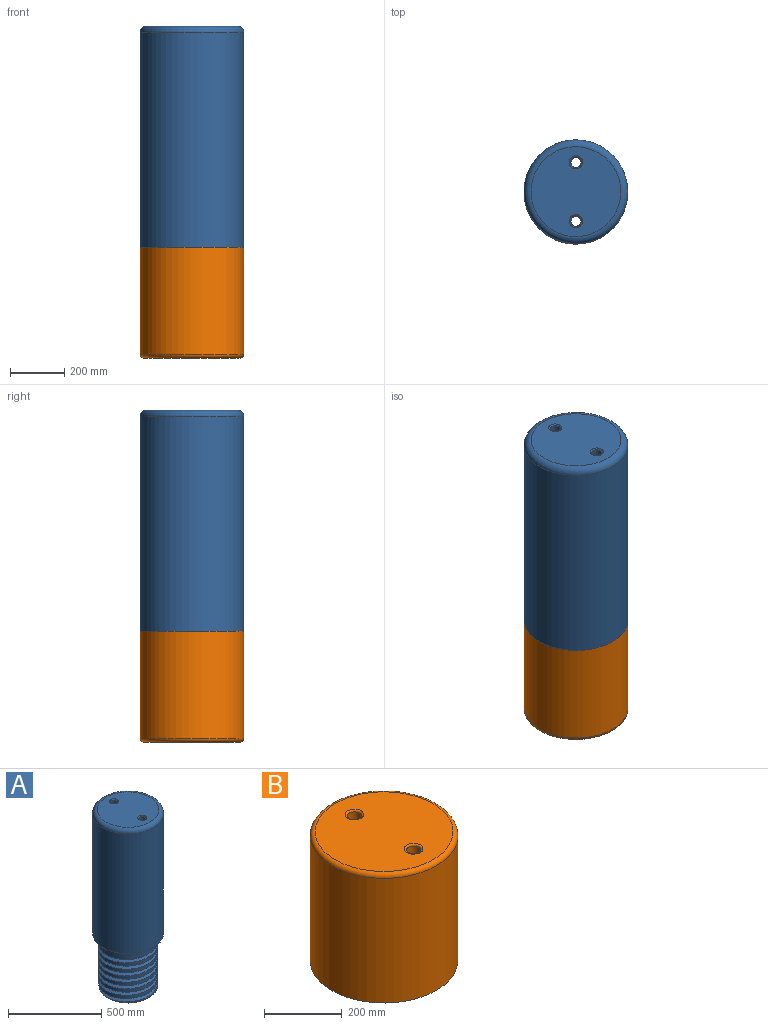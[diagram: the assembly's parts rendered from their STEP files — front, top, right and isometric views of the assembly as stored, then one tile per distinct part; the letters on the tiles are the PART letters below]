
ASSEMBLY  parts=2 mates=1
PART A: 25 faces, bbox 413.1x413.1x1182.3 mm
  f0: cylinder r=158.75mm len=317.5mm, axis (0,0,1), area 66109.5mm2, adj f1,f10,f15,f16
  f1: cylinder r=158.75mm len=317.5mm, axis (0,0,1), area 22484.7mm2, adj f0,f2,f16,f17
  f2: cylinder r=158.75mm len=317.5mm, axis (0,0,1), area 22483.1mm2, adj f1,f3,f16,f17
  f3: cylinder r=158.75mm len=317.5mm, axis (0,0,1), area 22485.4mm2, adj f2,f4,f16,f17
  f4: cylinder r=158.75mm len=317.5mm, axis (0,0,1), area 22483.2mm2, adj f3,f5,f16,f17
  f5: cylinder r=158.75mm len=317.5mm, axis (0,0,1), area 22482.8mm2, adj f4,f6,f16,f17
  f6: cylinder r=158.75mm len=317.5mm, axis (0,0,1), area 22438.2mm2, adj f5,f7,f14,f16,f17
  f7: cylinder r=158.75mm len=316.18mm, axis (0,0,1), area 4915.2mm2, adj f6,f14,f17
  f8: cylinder r=190.5mm len=787.4mm, axis (0,0,-1), area 942475.9mm2, adj f10,f18
  f9: plane 330.2x330.2mm, normal (0,0,1), area 81975.1mm2, adj f18,f23,f24
  f10: plane 381x381mm, normal (0,0,-1), area 34836.1mm2, adj f0,f8
  f11: plane 292.85x289.41mm, normal (0,0,-1), area 10854.2mm2, adj f13,f14,f16,f17
  f12: plane 266.7x266.7mm, normal (0,0,-1), area 52206.1mm2, adj f13,f21,f22
  f13: cylinder r=133.35mm len=1117.6mm, axis (0,0,1), area 936395.4mm2, adj f11,f12
  f14: cone r=146.05mm half-angle=45deg, axis (0,0,1), area 11945.9mm2, adj f6,f7,f11,f16,f17
  f15: plane 20.32x17.6mm, normal (0,-1,0), area 178.8mm2, adj f0,f16,f17
  f16: bspline ~317.5x317.5mm, area 134574.2mm2, adj f0,f1,f2,f3,f4,f5,f6,f11
  f17: bspline ~317.5x317.5mm, area 130072.8mm2, adj f1,f2,f3,f4,f5,f6,f7,f11
  f18: torus R=165.1mm, axis (0,0,1), area 45442.2mm2, adj f8,f9
  f19: cylinder r=19.05mm len=40.64mm, axis (0,0,1), area 4864.4mm2, adj f22,f23
  f20: cylinder r=19.05mm len=40.64mm, axis (0,0,1), area 4864.4mm2, adj f21,f24
  f21: torus R=24.13mm, axis (0,0,1), area 1047.7mm2, adj f12,f20
  f22: torus R=24.13mm, axis (0,0,1), area 1047.7mm2, adj f12,f19
  f23: torus R=24.13mm, axis (0,0,1), area 1047.7mm2, adj f9,f19
  f24: torus R=24.13mm, axis (0,0,1), area 1047.7mm2, adj f9,f20
PART B: 23 faces, bbox 412.9x412.9x419.8 mm
  f0: cylinder r=158.75mm len=317.5mm, axis (0,0,1), area 44336.9mm2, adj f1,f11,f15,f16
  f1: cylinder r=158.75mm len=317.5mm, axis (0,0,1), area 24067.8mm2, adj f0,f2,f14,f15
  f2: cylinder r=158.75mm len=317.5mm, axis (0,0,1), area 24069.5mm2, adj f1,f3,f14,f15
  f3: cylinder r=158.75mm len=317.5mm, axis (0,0,1), area 24065.6mm2, adj f2,f4,f14,f15
  f4: cylinder r=158.75mm len=317.5mm, axis (0,0,1), area 24068.2mm2, adj f3,f5,f14,f15
  f5: cylinder r=158.75mm len=317.5mm, axis (0,0,1), area 24066.7mm2, adj f4,f6,f14,f15
  f6: cylinder r=158.75mm len=317.5mm, axis (0,0,1), area 24066.8mm2, adj f5,f7,f14,f15
  f7: cylinder r=158.75mm len=317.5mm, axis (0,0,1), area 11693.5mm2, adj f6,f12,f14,f15
  f8: cylinder r=190.5mm len=393.7mm, axis (0,0,-1), area 471238mm2, adj f10,f13
  f9: plane 355.6x355.6mm, normal (0,0,1), area 95656.2mm2, adj f13,f19,f20
  f10: plane 381.49x381.49mm, normal (0,0,-1), area 21323mm2, adj f8,f12,f14,f15
  f11: plane 317.5x317.5mm, normal (0,0,-1), area 75514.6mm2, adj f0,f21,f22
  f12: cone r=171.45mm half-angle=45deg, axis (0,0,-1), area 13228.4mm2, adj f7,f10,f14,f15
  f13: torus R=177.8mm, axis (0,0,1), area 23299.6mm2, adj f8,f9
  f14: bspline ~352.7x352.7mm, area 151110.6mm2, adj f1,f2,f3,f4,f5,f6,f7,f10
  f15: bspline ~352.7x352.7mm, area 155914.8mm2, adj f0,f1,f2,f3,f4,f5,f6,f7
  f16: plane 20.32x17.6mm, normal (0,-1,0), area 178.8mm2, adj f0,f14,f15
  f17: cylinder r=19.05mm len=40.64mm, axis (0,0,1), area 4864.4mm2, adj f19,f22
  f18: cylinder r=19.05mm len=40.64mm, axis (0,0,1), area 4864.4mm2, adj f20,f21
  f19: torus R=24.13mm, axis (0,0,1), area 1047.7mm2, adj f9,f17
  f20: torus R=24.13mm, axis (0,0,1), area 1047.7mm2, adj f9,f18
  f21: torus R=24.13mm, axis (0,0,1), area 1047.7mm2, adj f11,f18
  f22: torus R=24.13mm, axis (0,0,1), area 1047.7mm2, adj f11,f17
PLACE A at identity
PLACE B rot(axis=(1,0,0),180deg) t=(0,0,-1117.6)mm
MATE fastened B.f8 <-> A.f8  axis (0,0,1) through (0,0,-762)mm
